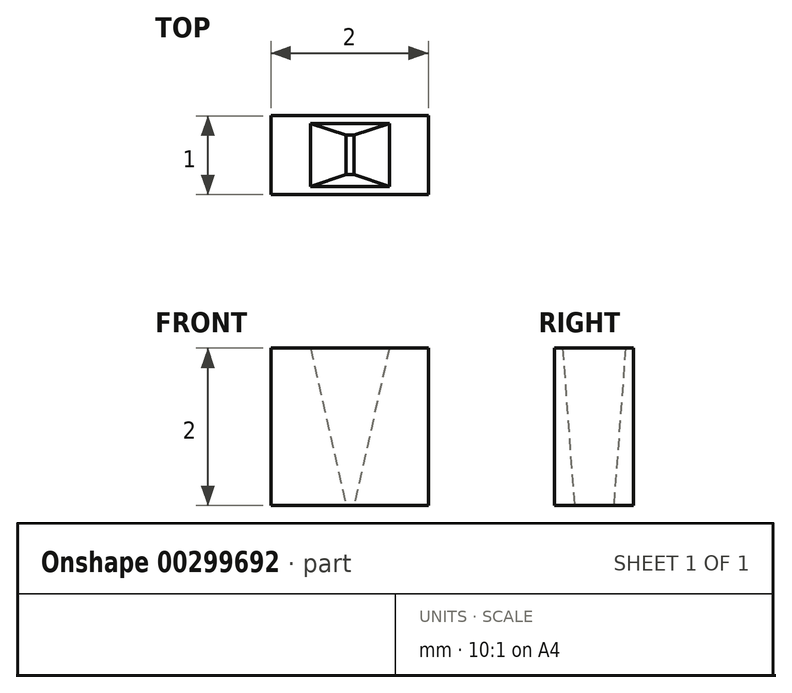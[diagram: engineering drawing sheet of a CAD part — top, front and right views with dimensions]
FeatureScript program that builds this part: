
annotation { "Feature Type Name" : "Feature", "Feature Type Description" : "" }
export const myFeature = defineFeature(function(context is Context, id is Id, definition is map)
    precondition{}
    {
        {
            var Q0;
            Q0=qCreatedBy(makeId("Top.planeOp"),FACE);
            var sketch = newSketch(context, id + "F0", { "sketchPlane" : qUnion([Q0])});
            skLineSegment(sketch, "E0.bottom", {"start": v(54.81, -38.39) * mm, "end": v(56.81, -38.39) * mm});
            skLineSegment(sketch, "E0.top", {"start": v(54.81, -39.39) * mm, "end": v(56.81, -39.39) * mm});
            skLineSegment(sketch, "E0.left", {"start": v(54.81, -38.39) * mm, "end": v(54.81, -39.39) * mm});
            skLineSegment(sketch, "E0.right", {"start": v(56.81, -38.39) * mm, "end": v(56.81, -39.39) * mm});
            skSolve(sketch);
        }
        {
            var Q0;
            Q0=makeQuery(id+"F0.imprint","IMPRINT",FACE,{"disambiguationData":[TD([[makeQuery(id+"F0.imprint","IMPRINT",EDGE,{"derivedFrom":sQuery(id+"F0.wireOp",EDGE,"E0.bottom")}),-1.0]])]});
            extrude(context, id + "F1", {"entities" : qUnion([Q0]), "depth" : 2 * mm});
        }
        {
            var Q0;
            Q0=makeQuery(id+"F1.opExtrude","CAP_FACE",FACE,{"disambiguationData":[OSD([sQuery(id+"F0.wireOp",EDGE,"E0.bottom"),sQuery(id+"F0.wireOp",EDGE,"E0.top"),sQuery(id+"F0.wireOp",EDGE,"E0.left"),sQuery(id+"F0.wireOp",EDGE,"E0.right")])],"isStart":false});
            var sketch = newSketch(context, id + "F2", { "sketchPlane" : qUnion([Q0])});
            skPoint(sketch, "E1.oppositeSnap0", {"position": v(56.81, -39.29) * mm});
            skLineSegment(sketch, "E1.bottom", {"start": v(55.31, -38.49) * mm, "end": v(56.31, -38.49) * mm});
            skLineSegment(sketch, "E1.top", {"start": v(55.31, -39.29) * mm, "end": v(56.31, -39.29) * mm});
            skLineSegment(sketch, "E1.left", {"start": v(55.31, -38.49) * mm, "end": v(55.31, -39.29) * mm});
            skLineSegment(sketch, "E1.right", {"start": v(56.31, -38.49) * mm, "end": v(56.31, -39.29) * mm});
            skSolve(sketch);
        }
        {
            var Q0;
            Q0=makeQuery(id+"F1.opExtrude","CAP_FACE",FACE,{"disambiguationData":[OSD([sQuery(id+"F0.wireOp",EDGE,"E0.bottom"),sQuery(id+"F0.wireOp",EDGE,"E0.top"),sQuery(id+"F0.wireOp",EDGE,"E0.left"),sQuery(id+"F0.wireOp",EDGE,"E0.right")])],"isStart":true});
            var sketch = newSketch(context, id + "F3", { "sketchPlane" : qUnion([Q0])});
            skLineSegment(sketch, "E2.bottom", {"start": v(55.76, 39.14) * mm, "end": v(55.86, 39.14) * mm});
            skLineSegment(sketch, "E2.top", {"start": v(55.76, 38.64) * mm, "end": v(55.86, 38.64) * mm});
            skLineSegment(sketch, "E2.left", {"start": v(55.76, 39.14) * mm, "end": v(55.76, 38.64) * mm});
            skLineSegment(sketch, "E2.right", {"start": v(55.86, 39.14) * mm, "end": v(55.86, 38.64) * mm});
            skSolve(sketch);
        }
        {
            var Q1;
            Q1 = qSketchRegion(id + "F2", true);
            var Q2;
            Q2 = qSketchRegion(id + "F3", true);
            var Q3;
            Q3=sQuery(id+"F3.wireOp",VERTEX,"E2.left.end");
            var Q4;
            Q4=sQuery(id+"F2.wireOp",VERTEX,"E1.left.start");
            loft(context, id + "F4", {"operationType" : NewBodyOperationType.REMOVE, "sheetProfilesArray" : [{ "sheetProfileEntities" : qUnion([Q1]) }, { "sheetProfileEntities" : qUnion([Q2]) }], "matchConnections" : true, "connections" : [{ "connectionEntities" : qUnion([Q3, Q4]), "connectionEdgeQueries" : qUnion([]), "connectionEdgeParameters" : [] }]});
        }
    });
